# Revit family: Urinal-Wall_Mount-KOHLER-PATIO-K-18645A_1
name_source: partatom
category: Plumbing Fixtures
units: mm (PartAtom-declared; Revit-internal decimal feet)

## family parameters
Cut with Voids When Loaded = No
Host = Face
OmniClass Number = 23.31.21.00
OmniClass Title = Urinals
Part Type = Normal
Room Calculation Point = No
Round Connector Dimension = Use Diameter
Shared = No

## types (1)
- 0-White
    ADA Compliant = No
    Assembly Code = D2010200
    CW Connection = Yes
    Cold Water Inlet = Cold Water Inlet
    Date Modified = 01/02/2023
    Default Elevation = 0"
    Description = URINAL 0.5L ANTI-MICROBIAL(REAR)
    Finish = Kohler-Vitreous_China-0-White
    Flow Rate = 0 GPM
    Flush Rate- GPF = 0 GPF
    Flush Rate- LPF = 0 LPF
    HW Connection = No
    Height = 25 1/4"
    Hot Water Inlet = Hot Water Inlet
    Length = 13 3/16"
    Manufacturer = Kohler Co.
    Master Format 2014 = 22 41 13.16
    Master Format 2014 Name = Residential Urinals
    Material = Vitreous China
    Model = K-18645A-0
    Pressure = 0.00 psi
    Product Name = PATIO
    Type = 1
    URL = https://www.kohlerasiapacific.com
    Vent Connection = No
    Waste Connection = Yes
    Waste Water Outlet = Waste Water Outlet
    WaterSense Certified = No
    Width = 13 3/16"

## geometry (parser evidence)
native form markers: Sweep x5
no freeform markers — native parametric forms only
